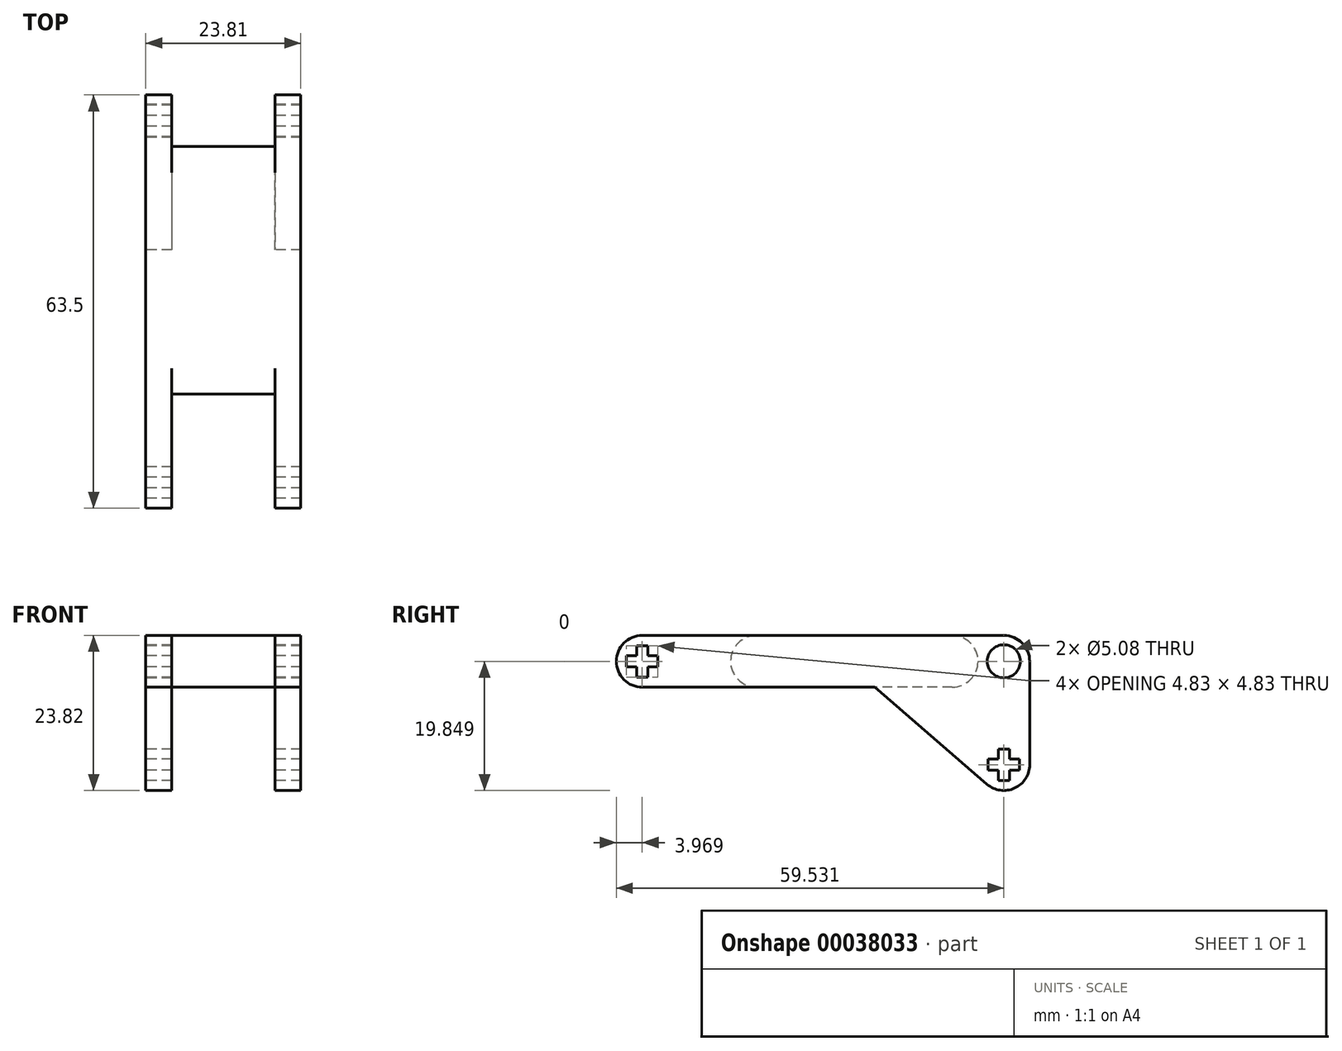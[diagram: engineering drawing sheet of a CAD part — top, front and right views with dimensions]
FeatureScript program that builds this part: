
annotation { "Feature Type Name" : "Feature", "Feature Type Description" : "" }
export const myFeature = defineFeature(function(context is Context, id is Id, definition is map)
    precondition{}
    {
        {
            var Q0;
            Q0=qCreatedBy(makeId("Top.planeOp"),FACE);
            var sketch = newSketch(context, id + "F0", { "sketchPlane" : qUnion([Q0])});
            skLineSegment(sketch, "E0.bottom", {"start": v(0, 0) * mm, "end": v(3.97, 0) * mm});
            skLineSegment(sketch, "E0.left", {"start": v(0, 0) * mm, "end": v(0, 63.5) * mm});
            skLineSegment(sketch, "E0.right", {"start": v(3.97, 0) * mm, "end": v(3.97, 17.56) * mm});
            skLineSegment(sketch, "E1.bottom", {"start": v(19.84, 0) * mm, "end": v(23.81, 0) * mm});
            skLineSegment(sketch, "E1.left", {"start": v(19.84, 0) * mm, "end": v(19.84, 17.56) * mm});
            skLineSegment(sketch, "E1.right", {"start": v(23.81, 0) * mm, "end": v(23.81, 63.5) * mm});
            skLineSegment(sketch, "E2", {"start": v(3.97, 17.56) * mm, "end": v(19.84, 17.56) * mm});
            skLineSegment(sketch, "E3", {"start": v(0, 63.5) * mm, "end": v(3.97, 63.5) * mm});
            skLineSegment(sketch, "E4", {"start": v(3.97, 63.5) * mm, "end": v(3.97, 55.56) * mm});
            skLineSegment(sketch, "E5", {"start": v(3.97, 55.56) * mm, "end": v(19.84, 55.56) * mm});
            skLineSegment(sketch, "E6", {"start": v(19.84, 55.56) * mm, "end": v(19.84, 63.5) * mm});
            skLineSegment(sketch, "E7", {"start": v(19.84, 63.5) * mm, "end": v(23.81, 63.5) * mm});
            skSolve(sketch);
        }
        {
            var Q0;
            Q0 = qSketchRegion(id + "F0", true);
            extrude(context, id + "F1", {"entities" : qUnion([Q0]), "depth" : 7.94 * mm});
        }
        {
            var Q0;
            Q0=makeQuery(id+"F1.opExtrude","CAP_EDGE",EDGE,{"disambiguationData":[OSD([sQuery(id+"F0.wireOp",EDGE,"E5")])],"isStart":false});
            var Q1;
            Q1=makeQuery(id+"F1.opExtrude","CAP_EDGE",EDGE,{"disambiguationData":[OSD([sQuery(id+"F0.wireOp",EDGE,"E5")])],"isStart":true});
            var Q2;
            Q2=makeQuery(id+"F1.opExtrude","CAP_EDGE",EDGE,{"disambiguationData":[OSD([sQuery(id+"F0.wireOp",EDGE,"E3")])],"isStart":false});
            var Q3;
            Q3=makeQuery(id+"F1.opExtrude","CAP_EDGE",EDGE,{"disambiguationData":[OSD([sQuery(id+"F0.wireOp",EDGE,"E7")])],"isStart":false});
            var Q4;
            Q4=makeQuery(id+"F1.opExtrude","CAP_EDGE",EDGE,{"disambiguationData":[OSD([sQuery(id+"F0.wireOp",EDGE,"E0.bottom")])],"isStart":false});
            var Q5;
            Q5=makeQuery(id+"F1.opExtrude","CAP_EDGE",EDGE,{"disambiguationData":[OSD([sQuery(id+"F0.wireOp",EDGE,"E0.bottom")])],"isStart":true});
            var Q6;
            Q6=makeQuery(id+"F1.opExtrude","CAP_EDGE",EDGE,{"disambiguationData":[OSD([sQuery(id+"F0.wireOp",EDGE,"E1.bottom")])],"isStart":false});
            var Q7;
            Q7=makeQuery(id+"F1.opExtrude","CAP_EDGE",EDGE,{"disambiguationData":[OSD([sQuery(id+"F0.wireOp",EDGE,"E1.bottom")])],"isStart":true});
            var Q8;
            Q8=makeQuery(id+"F1.opExtrude","CAP_EDGE",EDGE,{"disambiguationData":[OSD([sQuery(id+"F0.wireOp",EDGE,"E2")])],"isStart":false});
            var Q9;
            Q9=makeQuery(id+"F1.opExtrude","CAP_EDGE",EDGE,{"disambiguationData":[OSD([sQuery(id+"F0.wireOp",EDGE,"E2")])],"isStart":true});
            fillet(context, id + "F2", {"entities" : qUnion([Q0, Q1, Q2, Q3, Q4, Q5, Q6, Q7, Q8, Q9]), "radius" : 3.97 * mm, "tangentPropagation" : true, "allowEdgeOverflow" : false});
        }
        {
            var Q0;
            Q0=makeQuery(id+"F1.opExtrude","CAP_FACE",FACE,{"disambiguationData":[OSD([sQuery(id+"F0.wireOp",EDGE,"E0.bottom"),sQuery(id+"F0.wireOp",EDGE,"E0.left"),sQuery(id+"F0.wireOp",EDGE,"E0.right"),sQuery(id+"F0.wireOp",EDGE,"E1.bottom"),sQuery(id+"F0.wireOp",EDGE,"E1.left"),sQuery(id+"F0.wireOp",EDGE,"E1.right"),sQuery(id+"F0.wireOp",EDGE,"E2"),sQuery(id+"F0.wireOp",EDGE,"E3"),sQuery(id+"F0.wireOp",EDGE,"E4"),sQuery(id+"F0.wireOp",EDGE,"E5"),sQuery(id+"F0.wireOp",EDGE,"E6"),sQuery(id+"F0.wireOp",EDGE,"E7")])],"isStart":true});
            var sketch = newSketch(context, id + "F3", { "sketchPlane" : qUnion([Q0])});
            skLineSegment(sketch, "E8.bottom", {"start": v(23.81, -63.5) * mm, "end": v(19.84, -63.5) * mm});
            skLineSegment(sketch, "E8.top", {"start": v(23.81, -39.69) * mm, "end": v(19.84, -39.69) * mm});
            skLineSegment(sketch, "E8.left", {"start": v(23.81, -63.5) * mm, "end": v(23.81, -39.69) * mm});
            skLineSegment(sketch, "E8.right", {"start": v(19.84, -63.5) * mm, "end": v(19.84, -39.69) * mm});
            skLineSegment(sketch, "E9.bottom", {"start": v(3.97, -63.5) * mm, "end": v(0, -63.5) * mm});
            skLineSegment(sketch, "E9.top", {"start": v(3.97, -39.69) * mm, "end": v(0, -39.69) * mm});
            skLineSegment(sketch, "E9.left", {"start": v(3.97, -63.5) * mm, "end": v(3.97, -39.69) * mm});
            skLineSegment(sketch, "E9.right", {"start": v(0, -63.5) * mm, "end": v(0, -39.69) * mm});
            skSolve(sketch);
        }
        {
            var Q0;
            Q0 = qSketchRegion(id + "F3", true);
            extrude(context, id + "F4", {"entities" : qUnion([Q0]), "operationType" : NewBodyOperationType.ADD, "depth" : 15.88 * mm});
        }
        {
            var Q0;
            Q0=makeQuery(id+"F1.opExtrude","SWEPT_FACE",FACE,{"disambiguationData":[OSD([sQuery(id+"F0.wireOp",EDGE,"E0.left")])]});
            var sketch = newSketch(context, id + "F5", { "sketchPlane" : qUnion([Q0])});
            skLineSegment(sketch, "E10.rect.bottom", {"start": v(-6.38, 3.12) * mm, "end": v(-1.56, 3.12) * mm});
            skLineSegment(sketch, "E10.rect.top", {"start": v(-6.38, 4.81) * mm, "end": v(-1.56, 4.81) * mm});
            skLineSegment(sketch, "E10.rect.left", {"start": v(-6.38, 3.12) * mm, "end": v(-6.38, 4.81) * mm});
            skLineSegment(sketch, "E10.rect.right", {"start": v(-1.56, 3.12) * mm, "end": v(-1.56, 4.81) * mm});
            skPoint(sketch, "E10.rect.middle", {"position": v(-3.97, 3.97) * mm});
            skLineSegment(sketch, "E11.rect.bottom", {"start": v(-3.12, 1.56) * mm, "end": v(-4.81, 1.56) * mm});
            skLineSegment(sketch, "E11.rect.top", {"start": v(-3.12, 6.38) * mm, "end": v(-4.81, 6.38) * mm});
            skLineSegment(sketch, "E11.rect.left", {"start": v(-3.12, 1.56) * mm, "end": v(-3.12, 6.38) * mm});
            skLineSegment(sketch, "E11.rect.right", {"start": v(-4.81, 1.56) * mm, "end": v(-4.81, 6.38) * mm});
            skLineSegment(sketch, "E12.bottom", {"start": v(-39.69, 0) * mm, "end": v(-63.5, 0) * mm, "construction": true});
            skLineSegment(sketch, "E12.top", {"start": v(-39.69, -15.87) * mm, "end": v(-63.5, -15.87) * mm});
            skLineSegment(sketch, "E12.left", {"start": v(-39.69, 0) * mm, "end": v(-39.69, -15.87) * mm});
            skLineSegment(sketch, "E12.right", {"start": v(-63.5, 0) * mm, "end": v(-63.5, -15.88) * mm});
            skArc(sketch, "E13", {"start": v(-63.5, -11.9) * mm, "mid": v(-61.18, -15.52) * mm, "end": v(-56.94, -14.9) * mm});
            skLineSegment(sketch, "E14", {"start": v(-39.69, 0) * mm, "end": v(-56.94, -14.9) * mm});
            skLineSegment(sketch, "E15.rect.bottom", {"start": v(-57.12, -11.06) * mm, "end": v(-61.94, -11.06) * mm});
            skLineSegment(sketch, "E15.rect.top", {"start": v(-57.12, -12.75) * mm, "end": v(-61.94, -12.75) * mm});
            skLineSegment(sketch, "E15.rect.left", {"start": v(-57.12, -11.06) * mm, "end": v(-57.12, -12.75) * mm});
            skLineSegment(sketch, "E15.rect.right", {"start": v(-61.94, -11.06) * mm, "end": v(-61.94, -12.75) * mm});
            skLineSegment(sketch, "E16.rect.bottom", {"start": v(-60.38, -9.5) * mm, "end": v(-58.69, -9.5) * mm});
            skLineSegment(sketch, "E16.rect.top", {"start": v(-60.38, -14.32) * mm, "end": v(-58.69, -14.32) * mm});
            skLineSegment(sketch, "E16.rect.left", {"start": v(-60.38, -9.5) * mm, "end": v(-60.38, -14.32) * mm});
            skLineSegment(sketch, "E16.rect.right", {"start": v(-58.69, -9.5) * mm, "end": v(-58.69, -14.32) * mm});
            skCircle(sketch, "E17", {"center": v(-59.53, 3.97) * mm, "radius": 2.54 * mm});
            skSolve(sketch);
        }
        {
            var Q0;
            Q0 = qSketchRegion(id + "F5", true);
            var Q1;
            Q1=makeQuery(id+"F1.opExtrude","SWEPT_FACE",FACE,{"disambiguationData":[OSD([sQuery(id+"F0.wireOp",EDGE,"E1.right")])]});
            extrude(context, id + "F6", {"entities" : qUnion([Q0]), "operationType" : NewBodyOperationType.REMOVE, "endBound" : BoundingType.UP_TO_SURFACE, "oppositeDirection" : true, "endBoundEntityFace" : qUnion([Q1]), "depth" : 25.4 * mm});
        }
    });
